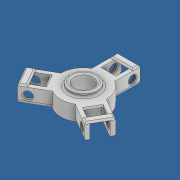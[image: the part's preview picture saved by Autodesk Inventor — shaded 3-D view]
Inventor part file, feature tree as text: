
AUTODESK INVENTOR PART (.ipt)
format: ipt  version: 2022 (Build 260153000, 153)  size: 414,208 bytes
history: native  units: in
note: dims shown in document units (in); Inventor stores cm internally (conversion verified against a paired STEP export)
features: sketch x10, extrude x9, chamfer x9, fillet x5, pattern_circular x1, shell x1, thread x1
ambient origin geometry x8: Origin, YZ Plane, XZ Plane, XY Plane, X Axis, Y Axis, Z Axis, Center Point
bodies: Solid1 (feature_tree)
feature tree (36):
  extrude  "Extrusion1"  Depth=3.9016in
  extrude  "Extrusion2"  Depth=0.3937in
  extrude  "Extrusion3"  Depth=0.3937in
  fillet  "Fillet4"  Radius=3.8583in
  extrude  "Extrusion8"  Depth=0.3937in TaperAngle=0.0deg
  chamfer  "Chamfer2"  Distance=0.7874in
  chamfer  "Chamfer3"  Distance=0.0394in
  pattern_circular  "Circular Pattern4"  Angle=45.0deg  [1 undecoded]
  sketch  "Sketch11"  dims[d16=0.0in]
  chamfer  "Chamfer4"  Distance=1.1811in Angle=360.0deg
  chamfer  "Chamfer5"  Distance=0.0492in Angle=45.0deg
  shell  "Shell1"  Thickness=0.0394in
  extrude  "Extrusion9"  Depth=0.0625in
  extrude  "Extrusion10"  Depth=0.0492in
  chamfer  "Chamfer6"  Distance=0.3937in
  chamfer  "Chamfer7"  Distance=0.5in
  fillet  "Fillet6"  Radius=0.3937in
  thread  "Thread2"  [1 undecoded]
  extrude  "Extrusion11"  Depth=0.0492in TaperAngle=45.0deg
  fillet  "Fillet7"  Radius=0.0354in
  extrude  "Extrusion13"  Depth=0.0492in TaperAngle=0.0deg
  extrude  "Extrusion14"  Depth=0.1181in TaperAngle=0.0deg
  chamfer  "Chamfer9"  Distance=0.0492in
  fillet  "Fillet9"  Radius=0.5in
  chamfer  "Chamfer10"  Distance=0.5906in
  fillet  "Fillet11"  Radius=0.0591in
  chamfer  "Chamfer11"  Distance=0.5in
  sketch  "Sketch1"  dims[d0=1.1811in d1=3.9016in]
  sketch  "Sketch2"  dims[d2=0.3937in d3=0.0in d4=0.2953in]
  sketch  "Sketch4"  dims[d5=0.689in d8=0.3937in d9=3.8583in]
  sketch  "Sketch10"  dims[d10=0.4921in d11=0.3937in d12=0.0in]
  sketch  "Sketch12"  dims[d17=0.1969in d18=0.7874in d19=0.0in]
  sketch  "Sketch13"  dims[d34=0.0197in]
  sketch  "Sketch14"  dims[d45=0.59in]
  sketch  "Sketch16"  dims[d46=0.1969in d47=0.0394in d48=0.0in]
  sketch  "Sketch17"  dims[d49=0.0394in d50=0.0492in d51=45.0deg d52=0.0394in d53=0.0492in d54=45.0deg d55=1.1811in d56=360.0deg d58=0.0394in d59=0.0492in d60=45.0deg d61=0.0394in d62=0.0492in d63=45.0deg d64=0.0625in d65=0.5in d66=0.3937in d67=0.0in d68=0.5in d69=0.3937in d70=0.0in d73=0.0394in d74=0.0492in d75=45.0deg d76=0.0394in d77=0.0492in d78=45.0deg d79=0.0354in d80=0.5512in d81=0.0in d82=0.1181in d83=0.0in d89=0.0492in d91=0.5in d92=0.5906in d93=0.0591in d94=0.0in d95=0.5in d96=0.0591in d97=0.0in d99=0.0394in d100=0.0492in d101=45.0deg d102=0.0787in d103=0.0394in d104=0.0492in d105=45.0deg d107=0.0787in d108=0.0394in d109=0.0492in d110=45.0deg]
note: 2 required parameter values undecoded (feature->parameter linkage not recoverable at this tier; creation-order binding heuristic only, values carry confidence <= 0.55)
